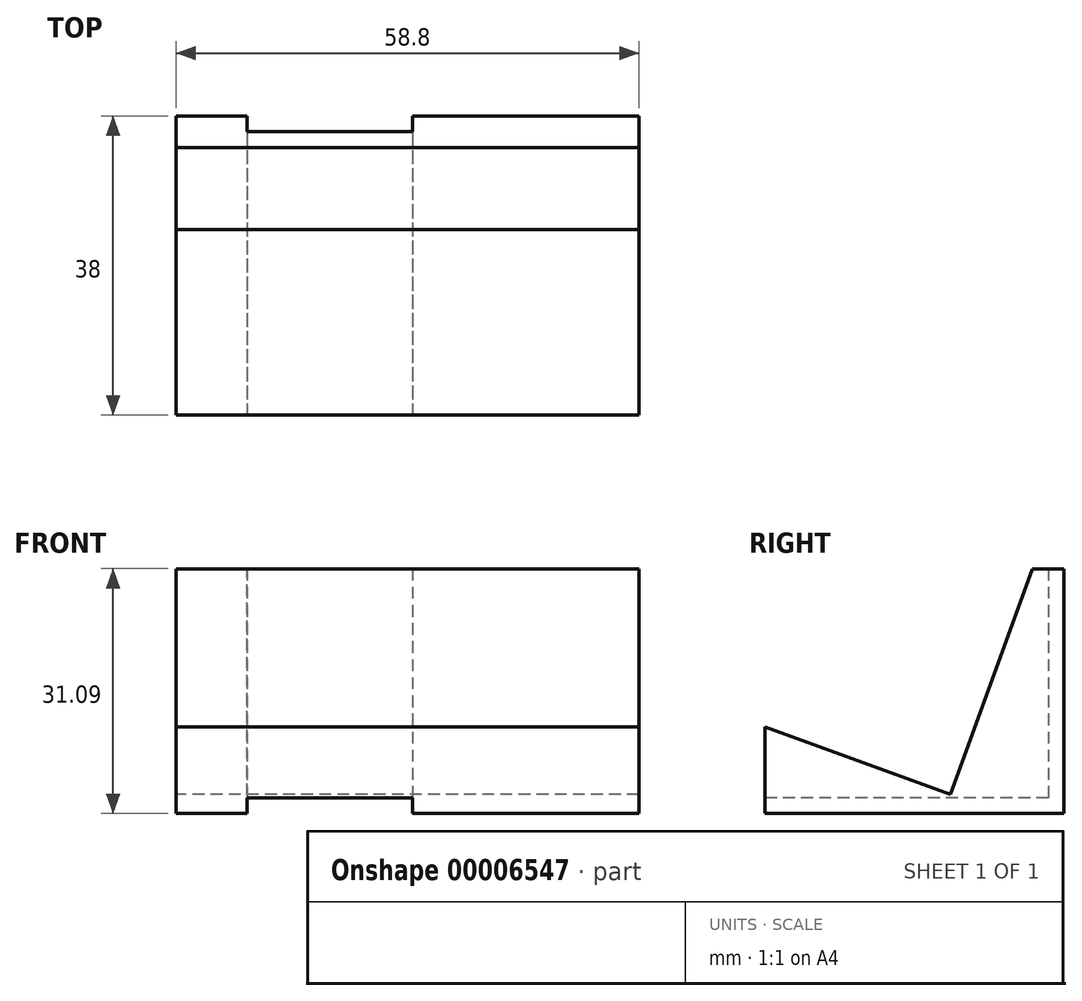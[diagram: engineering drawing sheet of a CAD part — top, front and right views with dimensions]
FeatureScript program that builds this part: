
annotation { "Feature Type Name" : "Feature", "Feature Type Description" : "" }
export const myFeature = defineFeature(function(context is Context, id is Id, definition is map)
    precondition{}
    {
        {
            var Q0;
            Q0=qCreatedBy(makeId("Right.planeOp"),FACE);
            var sketch = newSketch(context, id + "F0", { "sketchPlane" : qUnion([Q0])});
            skLineSegment(sketch, "E0", {"start": v(3.3, 36.04) * mm, "end": v(3.3, 67.13) * mm});
            skLineSegment(sketch, "E1", {"start": v(3.3, 67.13) * mm, "end": v(-7.14, 38.46) * mm});
            skLineSegment(sketch, "E2", {"start": v(-7.14, 38.46) * mm, "end": v(-30.7, 47.04) * mm});
            skLineSegment(sketch, "E3", {"start": v(-30.7, 47.04) * mm, "end": v(-30.7, 36.04) * mm});
            skLineSegment(sketch, "E4", {"start": v(-30.7, 36.04) * mm, "end": v(3.3, 36.04) * mm});
            skSolve(sketch);
        }
        {
            var Q0;
            Q0=qSketchRegion(id+"F0",true);
            var Q1;
            Q1 = qSketchRegion(id + "F2", true);
            extrude(context, id + "F1", {"entities" : qUnion([Q0, Q1]), "depth" : 58.8 * mm});
        }
        {
            var Q0;
            Q0=makeQuery(id+"F1.opExtrude","SWEPT_FACE",FACE,{"disambiguationData":[OSD([sQuery(id+"F0.wireOp",EDGE,"E3")])]});
            var sketch = newSketch(context, id + "F2", { "sketchPlane" : qUnion([Q0])});
            skLineSegment(sketch, "E5", {"start": v(30, 36.04) * mm, "end": v(30, 38.04) * mm});
            skLineSegment(sketch, "E6", {"start": v(30, 38.04) * mm, "end": v(9, 38.04) * mm});
            skLineSegment(sketch, "E7", {"start": v(9, 38.04) * mm, "end": v(9, 36.04) * mm});
            skSolve(sketch);
        }
        {
            var Q0;
            {var subQ2=sQuery(id+"F2.wireOp",EDGE,"E5");Q0=makeQuery(id+"F2.imprint","IMPRINT",FACE,{"disambiguationData":[TD([[makeQuery(id+"F2.imprint","IMPRINT",EDGE,{"derivedFrom":subQ2}),1.0]])]});}
            var Q1;
            Q1=makeQuery(id+"F1.opExtrude","SWEPT_FACE",FACE,{"disambiguationData":[OSD([sQuery(id+"F0.wireOp",EDGE,"E0")])]});
            extrude(context, id + "F3", {"entities" : qUnion([Q0]), "operationType" : NewBodyOperationType.REMOVE, "endBound" : BoundingType.UP_TO_SURFACE, "oppositeDirection" : true, "endBoundEntityFace" : qUnion([Q1]), "depth" : 25 * mm});
        }
        {
            var Q0;
            Q0=makeQuery(id+"F1.opExtrude","SWEPT_FACE",FACE,{"disambiguationData":[OSD([sQuery(id+"F0.wireOp",EDGE,"E0")])]});
            extrude(context, id + "F4", {"entities" : qUnion([Q0]), "operationType" : NewBodyOperationType.ADD, "depth" : 4 * mm});
        }
        {
            var Q0;
            {var subQ0=sQuery(id+"F2.wireOp",EDGE,"E6");Q0=makeQuery(id+"F4.boolean.opBoolean","MERGE",FACE,{"derivedFrom":[makeQuery(id+"F3.boolean.opBoolean","COPY",FACE,{"derivedFrom":makeQuery(id+"F3.opExtrude","SWEPT_FACE",FACE,{"disambiguationData":[OSD([subQ0])]})}),makeQuery(id+"F4.opExtrude","SWEPT_FACE",FACE,{"disambiguationData":[OSD([subQ0])]})]});}
            var sketch = newSketch(context, id + "F5", { "sketchPlane" : qUnion([Q0])});
            skLineSegment(sketch, "E8", {"start": v(30, -5.3) * mm, "end": v(9, -5.3) * mm});
            skSolve(sketch);
        }
        {
            var Q0;
            {var subQ3=sQuery(id+"F5.wireOp",EDGE,"E8");Q0=makeQuery(id+"F5.imprint","IMPRINT",FACE,{"disambiguationData":[TD([[makeQuery(id+"F5.imprint","IMPRINT",EDGE,{"derivedFrom":subQ3}),1.0]])]});}
            extrude(context, id + "F6", {"entities" : qUnion([Q0]), "operationType" : NewBodyOperationType.REMOVE, "endBound" : BoundingType.THROUGH_ALL, "oppositeDirection" : true, "depth" : 25 * mm});
        }
    });
